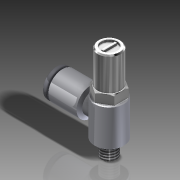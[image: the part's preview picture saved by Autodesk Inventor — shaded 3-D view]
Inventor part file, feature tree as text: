
AUTODESK INVENTOR PART (.ipt)
format: ipt  version: 2015 SP1 (Build 190201100, 201)  size: 221,184 bytes
history: native  units: in
note: dims shown in document units (in); Inventor stores cm internally (conversion verified against a paired STEP export)
features: other x1, imported_body x1, thread x1
ambient origin geometry x8: Origin, YZ Plane, XZ Plane, XY Plane, X Axis, Y Axis, Z Axis, Center Point
bodies: Body1 (feature_tree)
feature tree (3):
  parser-record x1  (decoder bookkeeping rows leaked as tree rows — omitted from the tree; the rows remain in map.json)
  imported_body  "Base1"
  thread  "Thread1"  [1 undecoded]
note: 1 required parameter value undecoded (feature->parameter linkage not recoverable at this tier; creation-order binding heuristic only, values carry confidence <= 0.55)
